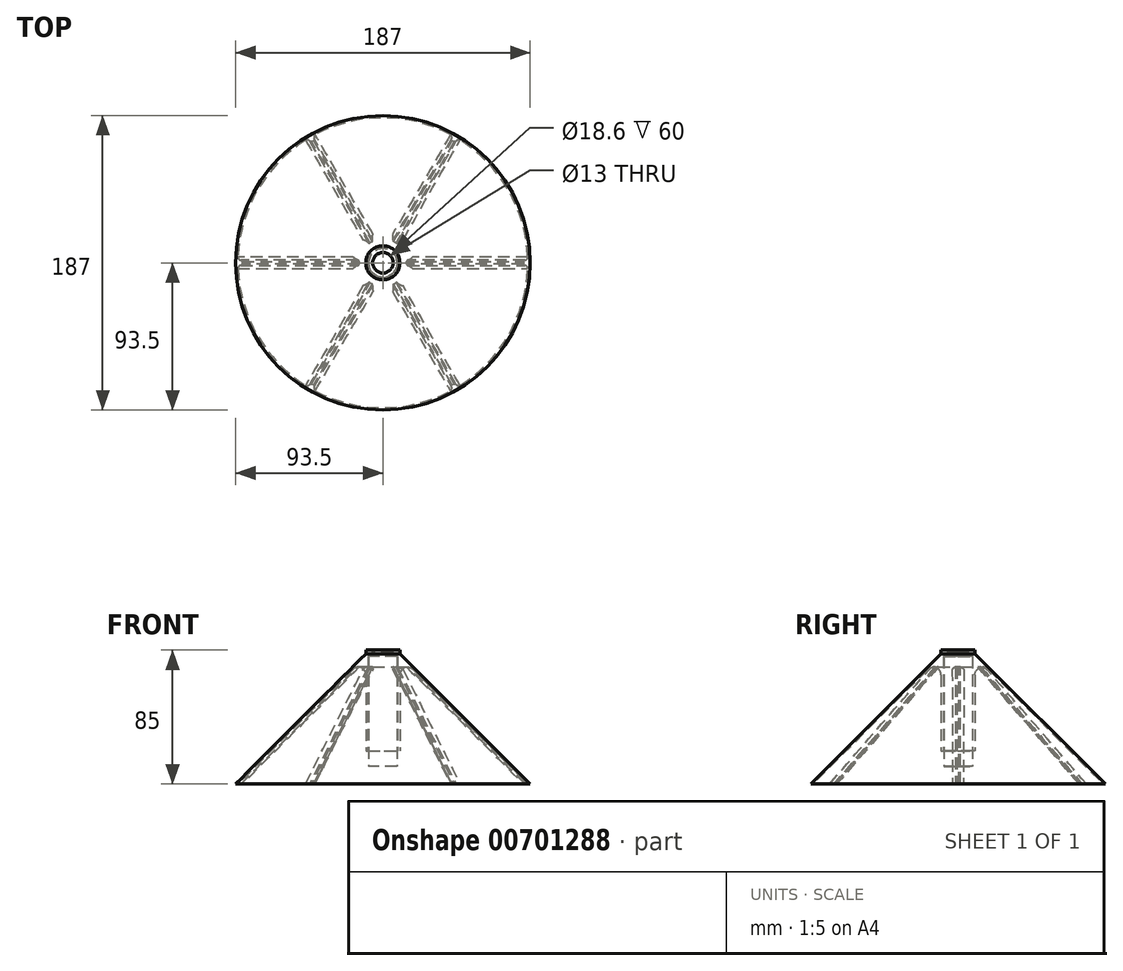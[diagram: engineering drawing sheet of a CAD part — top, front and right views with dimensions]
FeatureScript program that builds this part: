
annotation { "Feature Type Name" : "Feature", "Feature Type Description" : "" }
export const myFeature = defineFeature(function(context is Context, id is Id, definition is map)
    precondition{}
    {
        {
            var Q0;
            Q0=qCreatedBy(makeId("Top.planeOp"),FACE);
            var sketch = newSketch(context, id + "F0", { "sketchPlane" : qUnion([Q0])});
            skCircle(sketch, "E0", {"center": v(0, 0) * mm, "radius": 9 * mm});
            skSolve(sketch);
        }
        {
            var Q0;
            Q0 = qSketchRegion(id + "F0", true);
            extrude(context, id + "F1", {"entities" : qUnion([Q0]), "depth" : 70 * mm, "offsetDistance" : 25 * mm});
        }
        {
            var Q0;
            Q0=makeQuery(id+"F1.opExtrude","CAP_FACE",FACE,{"disambiguationData":[OSD([sQuery(id+"F0.wireOp",EDGE,"E0")])],"isStart":true});
            cPlane(context, id + "F2", {"entities" : qUnion([Q0]), "cplaneType" : CPlaneType.OFFSET, "offset" : 10 * mm, "oppositeDirection" : true, "width" : 150 * mm, "height" : 150 * mm});
        }
        {
            var Q0;
            Q0=qCreatedBy(id+"F2.planeOp",FACE);
            var sketch = newSketch(context, id + "F3", { "sketchPlane" : qUnion([Q0])});
            skCircle(sketch, "E1", {"center": v(0, 0) * mm, "radius": 9.3 * mm});
            skCircle(sketch, "E2", {"center": v(0, 0) * mm, "radius": 10.8 * mm});
            skSolve(sketch);
        }
        {
            var Q0;
            Q0=makeQuery(id+"F3.imprint","IMPRINT",FACE,{"disambiguationData":[TD([[makeQuery(id+"F3.imprint","IMPRINT",EDGE,{"derivedFrom":sQuery(id+"F3.wireOp",EDGE,"E1")}),-1.0]])]});
            var Q1;
            Q1=makeQuery(id+"F1.opExtrude","CAP_FACE",FACE,{"disambiguationData":[OSD([sQuery(id+"F0.wireOp",EDGE,"E0")])],"isStart":false});
            extrude(context, id + "F4", {"entities" : qUnion([Q0]), "endBound" : BoundingType.UP_TO_SURFACE, "oppositeDirection" : true, "depth" : 25 * mm, "endBoundEntityFace" : qUnion([Q1]), "offsetDistance" : 25 * mm});
        }
        {
            var Q0;
            Q0=qCreatedBy(makeId("Right.planeOp"),FACE);
            var sketch = newSketch(context, id + "F5", { "sketchPlane" : qUnion([Q0])});
            skLineSegment(sketch, "E3", {"start": v(-9, 70) * mm, "end": v(-5, 74) * mm});
            skLineSegment(sketch, "E4", {"start": v(-5, 74) * mm, "end": v(-10.8, 74) * mm});
            skLineSegment(sketch, "E5", {"start": v(-10.8, 74) * mm, "end": v(-10.8, 70) * mm});
            skLineSegment(sketch, "E6", {"start": v(-10.8, 10) * mm, "end": v(-10.8, 69.2) * mm, "construction": true});
            skLineSegment(sketch, "E7", {"start": v(-9, 0) * mm, "end": v(-9, 71.27) * mm, "construction": true});
            skLineSegment(sketch, "E8", {"start": v(-6.5, 74) * mm, "end": v(-6.5, 72.5) * mm});
            skLineSegment(sketch, "E9", {"start": v(-10.8, 70) * mm, "end": v(-9, 70) * mm});
            skLineSegment(sketch, "E10", {"start": v(0, 72.1) * mm, "end": v(0, -12.25) * mm, "construction": true});
            skSolve(sketch);
        }
        {
            var Q0;
            {var subQ0=sQuery(id+"F5.wireOp",EDGE,"E5");Q0=makeQuery(id+"F5.imprint","IMPRINT",FACE,{"disambiguationData":[TD([[makeQuery(id+"F5.imprint","IMPRINT",EDGE,{"derivedFrom":subQ0}),1.0]])]});}
            var Q1;
            Q1=sQuery(id+"F5.wireOp",EDGE,"E10");
            revolve(context, id + "F6", {"operationType" : NewBodyOperationType.ADD, "entities" : qUnion([Q0]), "axis" : qUnion([Q1]), "revolveType" : RevolveType.FULL});
        }
        {
            var Q0;
            Q0=qCreatedBy(makeId("Front.planeOp"),FACE);
            var sketch = newSketch(context, id + "F7", { "sketchPlane" : qUnion([Q0])});
            skLineSegment(sketch, "E11", {"start": v(-8.5, 74) * mm, "end": v(-93.5, -11) * mm});
            skLineSegment(sketch, "E12", {"start": v(6.5, 74) * mm, "end": v(6.5, 72.5) * mm});
            skLineSegment(sketch, "E13", {"start": v(-6.5, 72.5) * mm, "end": v(-6.5, 74) * mm});
            skLineSegment(sketch, "E14", {"start": v(-10.8, 70.29) * mm, "end": v(-92.09, -11) * mm});
            skLineSegment(sketch, "E15", {"start": v(-10.8, 10) * mm, "end": v(-10.8, 74) * mm});
            skLineSegment(sketch, "E16", {"start": v(10.8, 74) * mm, "end": v(10.8, 10) * mm});
            skLineSegment(sketch, "E17", {"start": v(-93.5, -11) * mm, "end": v(-92.09, -11) * mm});
            skLineSegment(sketch, "E18", {"start": v(0, 79.61) * mm, "end": v(0, -11.85) * mm, "construction": true});
            skSolve(sketch);
        }
        {
            var Q0;
            {var subQ4=sQuery(id+"F7.wireOp",EDGE,"E14");Q0=makeQuery(id+"F7.imprint","IMPRINT",FACE,{"disambiguationData":[TD([[makeQuery(id+"F7.imprint","IMPRINT",EDGE,{"derivedFrom":subQ4}),-1.0]])]});}
            var Q1;
            Q1=sQuery(id+"F7.wireOp",EDGE,"E18");
            revolve(context, id + "F8", {"operationType" : NewBodyOperationType.ADD, "entities" : qUnion([Q0]), "axis" : qUnion([Q1]), "revolveType" : RevolveType.FULL});
        }
        {
            var Q0;
            Q0=qCreatedBy(makeId("Front.planeOp"),FACE);
            var sketch = newSketch(context, id + "F9", { "sketchPlane" : qUnion([Q0])});
            skLineSegment(sketch, "E19", {"start": v(-9.8, 68.46) * mm, "end": v(-89.26, -11) * mm});
            skLineSegment(sketch, "E20", {"start": v(-92.09, -11) * mm, "end": v(-9.8, 71.29) * mm});
            skLineSegment(sketch, "E21", {"start": v(12.65, 68.43) * mm, "end": v(91.73, -10.65) * mm});
            skLineSegment(sketch, "E22", {"start": v(-92.09, -11) * mm, "end": v(-89.26, -11) * mm});
            skLineSegment(sketch, "E23", {"start": v(-9.8, 71.29) * mm, "end": v(-9.8, 68.46) * mm});
            skLineSegment(sketch, "E24", {"start": v(-10.8, 10) * mm, "end": v(-10.8, 68.08) * mm});
            skSolve(sketch);
        }
        {
            var Q0;
            Q0=makeQuery(id+"F8.opRevolve","SWEPT_EDGE",EDGE,{"disambiguationData":[OSD([sQuery(id+"F7.wireOp",EDGE,"E14"),sQuery(id+"F7.wireOp",EDGE,"E15")])]});
            fillet(context, id + "F10", {"entities" : qUnion([Q0]), "radius" : 5 * mm, "tangentPropagation" : true, "allowEdgeOverflow" : false});
        }
        {
            var Q0;
            Q0=makeQuery(id+"F9.imprint","IMPRINT",FACE,{"disambiguationData":[TD([[makeQuery(id+"F9.imprint","IMPRINT",EDGE,{"derivedFrom":sQuery(id+"F9.wireOp",EDGE,"E19")}),-1.0]])]});
            extrude(context, id + "F11", {"entities" : qUnion([Q0]), "endBound" : BoundingType.SYMMETRIC, "depth" : 3 * mm, "offsetDistance" : 25 * mm});
        }
        {
            var Q0;
            Q0=makeQuery(id+"F11.opExtrude","SWEPT_BODY",BODY,{"disambiguationData":[OSD([sQuery(id+"F9.wireOp",EDGE,"E19"),sQuery(id+"F9.wireOp",EDGE,"E20"),sQuery(id+"F9.wireOp",EDGE,"E22"),sQuery(id+"F9.wireOp",EDGE,"E23")])]});
            var Q1;
            Q1=makeQuery(id+"F1.opExtrude","CAP_EDGE",EDGE,{"disambiguationData":[OSD([sQuery(id+"F0.wireOp",EDGE,"E0")])],"isStart":true});
            circularPattern(context, id + "F12", {"entities" : qUnion([Q0]), "axis" : qUnion([Q1]), "angle" : 360 * degree, "instanceCount" : 6, "equalSpace" : true});
        }
        {
            var Q0;
            Q0=makeQuery(id+"F11.opExtrude","SWEPT_BODY",BODY,{"disambiguationData":[OSD([sQuery(id+"F9.wireOp",EDGE,"E19"),sQuery(id+"F9.wireOp",EDGE,"E20"),sQuery(id+"F9.wireOp",EDGE,"E22"),sQuery(id+"F9.wireOp",EDGE,"E23")])]});
            var Q1;
            Q1=makeQuery(id+"F12.opPattern","COPY",BODY,{"derivedFrom":makeQuery(id+"F11.opExtrude","SWEPT_BODY",BODY,{"disambiguationData":[OSD([sQuery(id+"F9.wireOp",EDGE,"E19"),sQuery(id+"F9.wireOp",EDGE,"E20"),sQuery(id+"F9.wireOp",EDGE,"E22"),sQuery(id+"F9.wireOp",EDGE,"E23")])]}),"instanceName":"2"});
            var Q2;
            Q2=makeQuery(id+"F12.opPattern","COPY",BODY,{"derivedFrom":makeQuery(id+"F11.opExtrude","SWEPT_BODY",BODY,{"disambiguationData":[OSD([sQuery(id+"F9.wireOp",EDGE,"E19"),sQuery(id+"F9.wireOp",EDGE,"E20"),sQuery(id+"F9.wireOp",EDGE,"E22"),sQuery(id+"F9.wireOp",EDGE,"E23")])]}),"instanceName":"4"});
            var Q3;
            Q3=makeQuery(id+"F12.opPattern","COPY",BODY,{"derivedFrom":makeQuery(id+"F11.opExtrude","SWEPT_BODY",BODY,{"disambiguationData":[OSD([sQuery(id+"F9.wireOp",EDGE,"E19"),sQuery(id+"F9.wireOp",EDGE,"E20"),sQuery(id+"F9.wireOp",EDGE,"E22"),sQuery(id+"F9.wireOp",EDGE,"E23")])]}),"instanceName":"5"});
            var Q4;
            Q4=makeQuery(id+"F12.opPattern","COPY",BODY,{"derivedFrom":makeQuery(id+"F11.opExtrude","SWEPT_BODY",BODY,{"disambiguationData":[OSD([sQuery(id+"F9.wireOp",EDGE,"E19"),sQuery(id+"F9.wireOp",EDGE,"E20"),sQuery(id+"F9.wireOp",EDGE,"E22"),sQuery(id+"F9.wireOp",EDGE,"E23")])]}),"instanceName":"3"});
            var Q5;
            Q5=makeQuery(id+"F12.opPattern","COPY",BODY,{"derivedFrom":makeQuery(id+"F11.opExtrude","SWEPT_BODY",BODY,{"disambiguationData":[OSD([sQuery(id+"F9.wireOp",EDGE,"E19"),sQuery(id+"F9.wireOp",EDGE,"E20"),sQuery(id+"F9.wireOp",EDGE,"E22"),sQuery(id+"F9.wireOp",EDGE,"E23")])]}),"instanceName":"1"});
            var Q6;
            Q6=makeQuery(id+"F4.opExtrude","SWEPT_BODY",BODY,{"disambiguationData":[OSD([sQuery(id+"F3.wireOp",EDGE,"E1"),sQuery(id+"F3.wireOp",EDGE,"E2")])]});
            booleanBodies(context, id + "F13", {"operationType" : BooleanOperationType.UNION, "tools" : qUnion([Q0, Q1, Q2, Q3, Q4, Q5, Q6])});
        }
        {
            var Q0;
            Q0=makeQuery(id+"F13.opBoolean","INTERSECT",EDGE,{"derivedFrom":[makeQuery(id+"F8.opRevolve","SWEPT_FACE",FACE,{"disambiguationData":[OSD([sQuery(id+"F7.wireOp",EDGE,"E14")])]}),makeQuery(id+"F11.opExtrude","CAP_FACE",FACE,{"disambiguationData":[OSD([sQuery(id+"F9.wireOp",EDGE,"E19"),sQuery(id+"F9.wireOp",EDGE,"E20"),sQuery(id+"F9.wireOp",EDGE,"E22"),sQuery(id+"F9.wireOp",EDGE,"E23")])],"isStart":true})]});
            var Q1;
            Q1=makeQuery(id+"F13.opBoolean","INTERSECT",EDGE,{"derivedFrom":[makeQuery(id+"F8.opRevolve","SWEPT_FACE",FACE,{"disambiguationData":[OSD([sQuery(id+"F7.wireOp",EDGE,"E14")])]}),makeQuery(id+"F12.opPattern","COPY",FACE,{"derivedFrom":makeQuery(id+"F11.opExtrude","CAP_FACE",FACE,{"disambiguationData":[OSD([sQuery(id+"F9.wireOp",EDGE,"E19"),sQuery(id+"F9.wireOp",EDGE,"E20"),sQuery(id+"F9.wireOp",EDGE,"E22"),sQuery(id+"F9.wireOp",EDGE,"E23")])],"isStart":false}),"instanceName":"5"})]});
            var Q2;
            Q2=makeQuery(id+"F13.opBoolean","INTERSECT",EDGE,{"derivedFrom":[makeQuery(id+"F8.opRevolve","SWEPT_FACE",FACE,{"disambiguationData":[OSD([sQuery(id+"F7.wireOp",EDGE,"E14")])]}),makeQuery(id+"F11.opExtrude","CAP_FACE",FACE,{"disambiguationData":[OSD([sQuery(id+"F9.wireOp",EDGE,"E19"),sQuery(id+"F9.wireOp",EDGE,"E20"),sQuery(id+"F9.wireOp",EDGE,"E22"),sQuery(id+"F9.wireOp",EDGE,"E23")])],"isStart":false})]});
            var Q3;
            Q3=makeQuery(id+"F13.opBoolean","INTERSECT",EDGE,{"derivedFrom":[makeQuery(id+"F8.opRevolve","SWEPT_FACE",FACE,{"disambiguationData":[OSD([sQuery(id+"F7.wireOp",EDGE,"E14")])]}),makeQuery(id+"F12.opPattern","COPY",FACE,{"derivedFrom":makeQuery(id+"F11.opExtrude","CAP_FACE",FACE,{"disambiguationData":[OSD([sQuery(id+"F9.wireOp",EDGE,"E19"),sQuery(id+"F9.wireOp",EDGE,"E20"),sQuery(id+"F9.wireOp",EDGE,"E22"),sQuery(id+"F9.wireOp",EDGE,"E23")])],"isStart":false}),"instanceName":"1"})]});
            var Q4;
            Q4=makeQuery(id+"F13.opBoolean","INTERSECT",EDGE,{"derivedFrom":[makeQuery(id+"F8.opRevolve","SWEPT_FACE",FACE,{"disambiguationData":[OSD([sQuery(id+"F7.wireOp",EDGE,"E14")])]}),makeQuery(id+"F12.opPattern","COPY",FACE,{"derivedFrom":makeQuery(id+"F11.opExtrude","CAP_FACE",FACE,{"disambiguationData":[OSD([sQuery(id+"F9.wireOp",EDGE,"E19"),sQuery(id+"F9.wireOp",EDGE,"E20"),sQuery(id+"F9.wireOp",EDGE,"E22"),sQuery(id+"F9.wireOp",EDGE,"E23")])],"isStart":true}),"instanceName":"2"})]});
            var Q5;
            Q5=makeQuery(id+"F13.opBoolean","INTERSECT",EDGE,{"derivedFrom":[makeQuery(id+"F8.opRevolve","SWEPT_FACE",FACE,{"disambiguationData":[OSD([sQuery(id+"F7.wireOp",EDGE,"E14")])]}),makeQuery(id+"F12.opPattern","COPY",FACE,{"derivedFrom":makeQuery(id+"F11.opExtrude","CAP_FACE",FACE,{"disambiguationData":[OSD([sQuery(id+"F9.wireOp",EDGE,"E19"),sQuery(id+"F9.wireOp",EDGE,"E20"),sQuery(id+"F9.wireOp",EDGE,"E22"),sQuery(id+"F9.wireOp",EDGE,"E23")])],"isStart":false}),"instanceName":"2"})]});
            var Q6;
            Q6=makeQuery(id+"F13.opBoolean","INTERSECT",EDGE,{"derivedFrom":[makeQuery(id+"F8.opRevolve","SWEPT_FACE",FACE,{"disambiguationData":[OSD([sQuery(id+"F7.wireOp",EDGE,"E14")])]}),makeQuery(id+"F12.opPattern","COPY",FACE,{"derivedFrom":makeQuery(id+"F11.opExtrude","CAP_FACE",FACE,{"disambiguationData":[OSD([sQuery(id+"F9.wireOp",EDGE,"E19"),sQuery(id+"F9.wireOp",EDGE,"E20"),sQuery(id+"F9.wireOp",EDGE,"E22"),sQuery(id+"F9.wireOp",EDGE,"E23")])],"isStart":true}),"instanceName":"3"})]});
            var Q7;
            Q7=makeQuery(id+"F13.opBoolean","INTERSECT",EDGE,{"derivedFrom":[makeQuery(id+"F8.opRevolve","SWEPT_FACE",FACE,{"disambiguationData":[OSD([sQuery(id+"F7.wireOp",EDGE,"E14")])]}),makeQuery(id+"F12.opPattern","COPY",FACE,{"derivedFrom":makeQuery(id+"F11.opExtrude","CAP_FACE",FACE,{"disambiguationData":[OSD([sQuery(id+"F9.wireOp",EDGE,"E19"),sQuery(id+"F9.wireOp",EDGE,"E20"),sQuery(id+"F9.wireOp",EDGE,"E22"),sQuery(id+"F9.wireOp",EDGE,"E23")])],"isStart":false}),"instanceName":"3"})]});
            var Q8;
            Q8=makeQuery(id+"F13.opBoolean","INTERSECT",EDGE,{"derivedFrom":[makeQuery(id+"F8.opRevolve","SWEPT_FACE",FACE,{"disambiguationData":[OSD([sQuery(id+"F7.wireOp",EDGE,"E14")])]}),makeQuery(id+"F12.opPattern","COPY",FACE,{"derivedFrom":makeQuery(id+"F11.opExtrude","CAP_FACE",FACE,{"disambiguationData":[OSD([sQuery(id+"F9.wireOp",EDGE,"E19"),sQuery(id+"F9.wireOp",EDGE,"E20"),sQuery(id+"F9.wireOp",EDGE,"E22"),sQuery(id+"F9.wireOp",EDGE,"E23")])],"isStart":true}),"instanceName":"4"})]});
            var Q9;
            Q9=makeQuery(id+"F13.opBoolean","INTERSECT",EDGE,{"derivedFrom":[makeQuery(id+"F8.opRevolve","SWEPT_FACE",FACE,{"disambiguationData":[OSD([sQuery(id+"F7.wireOp",EDGE,"E14")])]}),makeQuery(id+"F12.opPattern","COPY",FACE,{"derivedFrom":makeQuery(id+"F11.opExtrude","CAP_FACE",FACE,{"disambiguationData":[OSD([sQuery(id+"F9.wireOp",EDGE,"E19"),sQuery(id+"F9.wireOp",EDGE,"E20"),sQuery(id+"F9.wireOp",EDGE,"E22"),sQuery(id+"F9.wireOp",EDGE,"E23")])],"isStart":false}),"instanceName":"4"})]});
            var Q10;
            Q10=makeQuery(id+"F13.opBoolean","INTERSECT",EDGE,{"derivedFrom":[makeQuery(id+"F8.opRevolve","SWEPT_FACE",FACE,{"disambiguationData":[OSD([sQuery(id+"F7.wireOp",EDGE,"E14")])]}),makeQuery(id+"F12.opPattern","COPY",FACE,{"derivedFrom":makeQuery(id+"F11.opExtrude","CAP_FACE",FACE,{"disambiguationData":[OSD([sQuery(id+"F9.wireOp",EDGE,"E19"),sQuery(id+"F9.wireOp",EDGE,"E20"),sQuery(id+"F9.wireOp",EDGE,"E22"),sQuery(id+"F9.wireOp",EDGE,"E23")])],"isStart":true}),"instanceName":"5"})]});
            var Q11;
            Q11=makeQuery(id+"F13.opBoolean","INTERSECT",EDGE,{"derivedFrom":[makeQuery(id+"F8.opRevolve","SWEPT_FACE",FACE,{"disambiguationData":[OSD([sQuery(id+"F7.wireOp",EDGE,"E14")])]}),makeQuery(id+"F12.opPattern","COPY",FACE,{"derivedFrom":makeQuery(id+"F11.opExtrude","CAP_FACE",FACE,{"disambiguationData":[OSD([sQuery(id+"F9.wireOp",EDGE,"E19"),sQuery(id+"F9.wireOp",EDGE,"E20"),sQuery(id+"F9.wireOp",EDGE,"E22"),sQuery(id+"F9.wireOp",EDGE,"E23")])],"isStart":true}),"instanceName":"1"})]});
            fillet(context, id + "F14", {"entities" : qUnion([Q0, Q1, Q2, Q3, Q4, Q5, Q6, Q7, Q8, Q9, Q10, Q11]), "radius" : 2 * mm, "tangentPropagation" : true, "allowEdgeOverflow" : false});
        }
        {
            var Q0;
            {var subQ0=sQuery(id+"F9.wireOp",EDGE,"E19");Q0=makeQuery(id+"F14.opFillet","BLEND_EDGE",EDGE,{"blendedFrom":[makeQuery(id+"F13.opBoolean","INTERSECT",EDGE,{"derivedFrom":[makeQuery(id+"F8.opRevolve","SWEPT_FACE",FACE,{"disambiguationData":[OSD([sQuery(id+"F7.wireOp",EDGE,"E14")])]}),makeQuery(id+"F12.opPattern","COPY",FACE,{"derivedFrom":makeQuery(id+"F11.opExtrude","CAP_FACE",FACE,{"disambiguationData":[OSD([subQ0,sQuery(id+"F9.wireOp",EDGE,"E20"),sQuery(id+"F9.wireOp",EDGE,"E22"),sQuery(id+"F9.wireOp",EDGE,"E23")])],"isStart":true}),"instanceName":"5"})]}),makeQuery(id+"F12.opPattern","COPY",FACE,{"derivedFrom":makeQuery(id+"F11.opExtrude","SWEPT_FACE",FACE,{"disambiguationData":[OSD([subQ0])]}),"instanceName":"5"})],"blendedInto":[makeQuery(id+"F12.opPattern","COPY",FACE,{"derivedFrom":makeQuery(id+"F11.opExtrude","SWEPT_FACE",FACE,{"disambiguationData":[OSD([subQ0])]}),"instanceName":"5"})]});}
            var Q1;
            {var subQ0=sQuery(id+"F9.wireOp",EDGE,"E19");Q1=makeQuery(id+"F14.opFillet","BLEND_EDGE",EDGE,{"blendedFrom":[makeQuery(id+"F13.opBoolean","INTERSECT",EDGE,{"derivedFrom":[makeQuery(id+"F8.opRevolve","SWEPT_FACE",FACE,{"disambiguationData":[OSD([sQuery(id+"F7.wireOp",EDGE,"E14")])]}),makeQuery(id+"F12.opPattern","COPY",FACE,{"derivedFrom":makeQuery(id+"F11.opExtrude","CAP_FACE",FACE,{"disambiguationData":[OSD([subQ0,sQuery(id+"F9.wireOp",EDGE,"E20"),sQuery(id+"F9.wireOp",EDGE,"E22"),sQuery(id+"F9.wireOp",EDGE,"E23")])],"isStart":false}),"instanceName":"5"})]}),makeQuery(id+"F12.opPattern","COPY",FACE,{"derivedFrom":makeQuery(id+"F11.opExtrude","SWEPT_FACE",FACE,{"disambiguationData":[OSD([subQ0])]}),"instanceName":"5"})],"blendedInto":[makeQuery(id+"F12.opPattern","COPY",FACE,{"derivedFrom":makeQuery(id+"F11.opExtrude","SWEPT_FACE",FACE,{"disambiguationData":[OSD([subQ0])]}),"instanceName":"5"})]});}
            var Q2;
            {var subQ0=sQuery(id+"F9.wireOp",EDGE,"E19");Q2=makeQuery(id+"F14.opFillet","BLEND_EDGE",EDGE,{"blendedFrom":[makeQuery(id+"F13.opBoolean","INTERSECT",EDGE,{"derivedFrom":[makeQuery(id+"F8.opRevolve","SWEPT_FACE",FACE,{"disambiguationData":[OSD([sQuery(id+"F7.wireOp",EDGE,"E14")])]}),makeQuery(id+"F11.opExtrude","CAP_FACE",FACE,{"disambiguationData":[OSD([subQ0,sQuery(id+"F9.wireOp",EDGE,"E20"),sQuery(id+"F9.wireOp",EDGE,"E22"),sQuery(id+"F9.wireOp",EDGE,"E23")])],"isStart":true})]}),makeQuery(id+"F11.opExtrude","SWEPT_FACE",FACE,{"disambiguationData":[OSD([subQ0])]})],"blendedInto":[makeQuery(id+"F11.opExtrude","SWEPT_FACE",FACE,{"disambiguationData":[OSD([subQ0])]})]});}
            var Q3;
            {var subQ0=sQuery(id+"F9.wireOp",EDGE,"E19");Q3=makeQuery(id+"F14.opFillet","BLEND_EDGE",EDGE,{"blendedFrom":[makeQuery(id+"F13.opBoolean","INTERSECT",EDGE,{"derivedFrom":[makeQuery(id+"F8.opRevolve","SWEPT_FACE",FACE,{"disambiguationData":[OSD([sQuery(id+"F7.wireOp",EDGE,"E14")])]}),makeQuery(id+"F11.opExtrude","CAP_FACE",FACE,{"disambiguationData":[OSD([subQ0,sQuery(id+"F9.wireOp",EDGE,"E20"),sQuery(id+"F9.wireOp",EDGE,"E22"),sQuery(id+"F9.wireOp",EDGE,"E23")])],"isStart":false})]}),makeQuery(id+"F11.opExtrude","SWEPT_FACE",FACE,{"disambiguationData":[OSD([subQ0])]})],"blendedInto":[makeQuery(id+"F11.opExtrude","SWEPT_FACE",FACE,{"disambiguationData":[OSD([subQ0])]})]});}
            var Q4;
            {var subQ0=sQuery(id+"F9.wireOp",EDGE,"E19");Q4=makeQuery(id+"F14.opFillet","BLEND_EDGE",EDGE,{"blendedFrom":[makeQuery(id+"F13.opBoolean","INTERSECT",EDGE,{"derivedFrom":[makeQuery(id+"F8.opRevolve","SWEPT_FACE",FACE,{"disambiguationData":[OSD([sQuery(id+"F7.wireOp",EDGE,"E14")])]}),makeQuery(id+"F12.opPattern","COPY",FACE,{"derivedFrom":makeQuery(id+"F11.opExtrude","CAP_FACE",FACE,{"disambiguationData":[OSD([subQ0,sQuery(id+"F9.wireOp",EDGE,"E20"),sQuery(id+"F9.wireOp",EDGE,"E22"),sQuery(id+"F9.wireOp",EDGE,"E23")])],"isStart":true}),"instanceName":"1"})]}),makeQuery(id+"F12.opPattern","COPY",FACE,{"derivedFrom":makeQuery(id+"F11.opExtrude","SWEPT_FACE",FACE,{"disambiguationData":[OSD([subQ0])]}),"instanceName":"1"})],"blendedInto":[makeQuery(id+"F12.opPattern","COPY",FACE,{"derivedFrom":makeQuery(id+"F11.opExtrude","SWEPT_FACE",FACE,{"disambiguationData":[OSD([subQ0])]}),"instanceName":"1"})]});}
            var Q5;
            {var subQ0=sQuery(id+"F9.wireOp",EDGE,"E19");Q5=makeQuery(id+"F14.opFillet","BLEND_EDGE",EDGE,{"blendedFrom":[makeQuery(id+"F13.opBoolean","INTERSECT",EDGE,{"derivedFrom":[makeQuery(id+"F8.opRevolve","SWEPT_FACE",FACE,{"disambiguationData":[OSD([sQuery(id+"F7.wireOp",EDGE,"E14")])]}),makeQuery(id+"F12.opPattern","COPY",FACE,{"derivedFrom":makeQuery(id+"F11.opExtrude","CAP_FACE",FACE,{"disambiguationData":[OSD([subQ0,sQuery(id+"F9.wireOp",EDGE,"E20"),sQuery(id+"F9.wireOp",EDGE,"E22"),sQuery(id+"F9.wireOp",EDGE,"E23")])],"isStart":false}),"instanceName":"1"})]}),makeQuery(id+"F12.opPattern","COPY",FACE,{"derivedFrom":makeQuery(id+"F11.opExtrude","SWEPT_FACE",FACE,{"disambiguationData":[OSD([subQ0])]}),"instanceName":"1"})],"blendedInto":[makeQuery(id+"F12.opPattern","COPY",FACE,{"derivedFrom":makeQuery(id+"F11.opExtrude","SWEPT_FACE",FACE,{"disambiguationData":[OSD([subQ0])]}),"instanceName":"1"})]});}
            var Q6;
            {var subQ0=sQuery(id+"F9.wireOp",EDGE,"E19");Q6=makeQuery(id+"F14.opFillet","BLEND_EDGE",EDGE,{"blendedFrom":[makeQuery(id+"F13.opBoolean","INTERSECT",EDGE,{"derivedFrom":[makeQuery(id+"F8.opRevolve","SWEPT_FACE",FACE,{"disambiguationData":[OSD([sQuery(id+"F7.wireOp",EDGE,"E14")])]}),makeQuery(id+"F12.opPattern","COPY",FACE,{"derivedFrom":makeQuery(id+"F11.opExtrude","CAP_FACE",FACE,{"disambiguationData":[OSD([subQ0,sQuery(id+"F9.wireOp",EDGE,"E20"),sQuery(id+"F9.wireOp",EDGE,"E22"),sQuery(id+"F9.wireOp",EDGE,"E23")])],"isStart":true}),"instanceName":"2"})]}),makeQuery(id+"F12.opPattern","COPY",FACE,{"derivedFrom":makeQuery(id+"F11.opExtrude","SWEPT_FACE",FACE,{"disambiguationData":[OSD([subQ0])]}),"instanceName":"2"})],"blendedInto":[makeQuery(id+"F12.opPattern","COPY",FACE,{"derivedFrom":makeQuery(id+"F11.opExtrude","SWEPT_FACE",FACE,{"disambiguationData":[OSD([subQ0])]}),"instanceName":"2"})]});}
            var Q7;
            {var subQ0=sQuery(id+"F9.wireOp",EDGE,"E19");Q7=makeQuery(id+"F14.opFillet","BLEND_EDGE",EDGE,{"blendedFrom":[makeQuery(id+"F13.opBoolean","INTERSECT",EDGE,{"derivedFrom":[makeQuery(id+"F8.opRevolve","SWEPT_FACE",FACE,{"disambiguationData":[OSD([sQuery(id+"F7.wireOp",EDGE,"E14")])]}),makeQuery(id+"F12.opPattern","COPY",FACE,{"derivedFrom":makeQuery(id+"F11.opExtrude","CAP_FACE",FACE,{"disambiguationData":[OSD([subQ0,sQuery(id+"F9.wireOp",EDGE,"E20"),sQuery(id+"F9.wireOp",EDGE,"E22"),sQuery(id+"F9.wireOp",EDGE,"E23")])],"isStart":false}),"instanceName":"2"})]}),makeQuery(id+"F12.opPattern","COPY",FACE,{"derivedFrom":makeQuery(id+"F11.opExtrude","SWEPT_FACE",FACE,{"disambiguationData":[OSD([subQ0])]}),"instanceName":"2"})],"blendedInto":[makeQuery(id+"F12.opPattern","COPY",FACE,{"derivedFrom":makeQuery(id+"F11.opExtrude","SWEPT_FACE",FACE,{"disambiguationData":[OSD([subQ0])]}),"instanceName":"2"})]});}
            var Q8;
            {var subQ0=sQuery(id+"F9.wireOp",EDGE,"E19");Q8=makeQuery(id+"F14.opFillet","BLEND_EDGE",EDGE,{"blendedFrom":[makeQuery(id+"F13.opBoolean","INTERSECT",EDGE,{"derivedFrom":[makeQuery(id+"F8.opRevolve","SWEPT_FACE",FACE,{"disambiguationData":[OSD([sQuery(id+"F7.wireOp",EDGE,"E14")])]}),makeQuery(id+"F12.opPattern","COPY",FACE,{"derivedFrom":makeQuery(id+"F11.opExtrude","CAP_FACE",FACE,{"disambiguationData":[OSD([subQ0,sQuery(id+"F9.wireOp",EDGE,"E20"),sQuery(id+"F9.wireOp",EDGE,"E22"),sQuery(id+"F9.wireOp",EDGE,"E23")])],"isStart":true}),"instanceName":"3"})]}),makeQuery(id+"F12.opPattern","COPY",FACE,{"derivedFrom":makeQuery(id+"F11.opExtrude","SWEPT_FACE",FACE,{"disambiguationData":[OSD([subQ0])]}),"instanceName":"3"})],"blendedInto":[makeQuery(id+"F12.opPattern","COPY",FACE,{"derivedFrom":makeQuery(id+"F11.opExtrude","SWEPT_FACE",FACE,{"disambiguationData":[OSD([subQ0])]}),"instanceName":"3"})]});}
            var Q9;
            {var subQ0=sQuery(id+"F9.wireOp",EDGE,"E19");Q9=makeQuery(id+"F14.opFillet","BLEND_EDGE",EDGE,{"blendedFrom":[makeQuery(id+"F13.opBoolean","INTERSECT",EDGE,{"derivedFrom":[makeQuery(id+"F8.opRevolve","SWEPT_FACE",FACE,{"disambiguationData":[OSD([sQuery(id+"F7.wireOp",EDGE,"E14")])]}),makeQuery(id+"F12.opPattern","COPY",FACE,{"derivedFrom":makeQuery(id+"F11.opExtrude","CAP_FACE",FACE,{"disambiguationData":[OSD([subQ0,sQuery(id+"F9.wireOp",EDGE,"E20"),sQuery(id+"F9.wireOp",EDGE,"E22"),sQuery(id+"F9.wireOp",EDGE,"E23")])],"isStart":false}),"instanceName":"3"})]}),makeQuery(id+"F12.opPattern","COPY",FACE,{"derivedFrom":makeQuery(id+"F11.opExtrude","SWEPT_FACE",FACE,{"disambiguationData":[OSD([subQ0])]}),"instanceName":"3"})],"blendedInto":[makeQuery(id+"F12.opPattern","COPY",FACE,{"derivedFrom":makeQuery(id+"F11.opExtrude","SWEPT_FACE",FACE,{"disambiguationData":[OSD([subQ0])]}),"instanceName":"3"})]});}
            var Q10;
            {var subQ0=sQuery(id+"F9.wireOp",EDGE,"E19");Q10=makeQuery(id+"F14.opFillet","BLEND_EDGE",EDGE,{"blendedFrom":[makeQuery(id+"F13.opBoolean","INTERSECT",EDGE,{"derivedFrom":[makeQuery(id+"F8.opRevolve","SWEPT_FACE",FACE,{"disambiguationData":[OSD([sQuery(id+"F7.wireOp",EDGE,"E14")])]}),makeQuery(id+"F12.opPattern","COPY",FACE,{"derivedFrom":makeQuery(id+"F11.opExtrude","CAP_FACE",FACE,{"disambiguationData":[OSD([subQ0,sQuery(id+"F9.wireOp",EDGE,"E20"),sQuery(id+"F9.wireOp",EDGE,"E22"),sQuery(id+"F9.wireOp",EDGE,"E23")])],"isStart":true}),"instanceName":"4"})]}),makeQuery(id+"F12.opPattern","COPY",FACE,{"derivedFrom":makeQuery(id+"F11.opExtrude","SWEPT_FACE",FACE,{"disambiguationData":[OSD([subQ0])]}),"instanceName":"4"})],"blendedInto":[makeQuery(id+"F12.opPattern","COPY",FACE,{"derivedFrom":makeQuery(id+"F11.opExtrude","SWEPT_FACE",FACE,{"disambiguationData":[OSD([subQ0])]}),"instanceName":"4"})]});}
            var Q11;
            {var subQ0=sQuery(id+"F9.wireOp",EDGE,"E19");Q11=makeQuery(id+"F14.opFillet","BLEND_EDGE",EDGE,{"blendedFrom":[makeQuery(id+"F13.opBoolean","INTERSECT",EDGE,{"derivedFrom":[makeQuery(id+"F8.opRevolve","SWEPT_FACE",FACE,{"disambiguationData":[OSD([sQuery(id+"F7.wireOp",EDGE,"E14")])]}),makeQuery(id+"F12.opPattern","COPY",FACE,{"derivedFrom":makeQuery(id+"F11.opExtrude","CAP_FACE",FACE,{"disambiguationData":[OSD([subQ0,sQuery(id+"F9.wireOp",EDGE,"E20"),sQuery(id+"F9.wireOp",EDGE,"E22"),sQuery(id+"F9.wireOp",EDGE,"E23")])],"isStart":false}),"instanceName":"4"})]}),makeQuery(id+"F12.opPattern","COPY",FACE,{"derivedFrom":makeQuery(id+"F11.opExtrude","SWEPT_FACE",FACE,{"disambiguationData":[OSD([subQ0])]}),"instanceName":"4"})],"blendedInto":[makeQuery(id+"F12.opPattern","COPY",FACE,{"derivedFrom":makeQuery(id+"F11.opExtrude","SWEPT_FACE",FACE,{"disambiguationData":[OSD([subQ0])]}),"instanceName":"4"})]});}
            fillet(context, id + "F15", {"entities" : qUnion([Q0, Q1, Q2, Q3, Q4, Q5, Q6, Q7, Q8, Q9, Q10, Q11]), "radius" : 1 * mm, "tangentPropagation" : true, "allowEdgeOverflow" : false});
        }
    });
